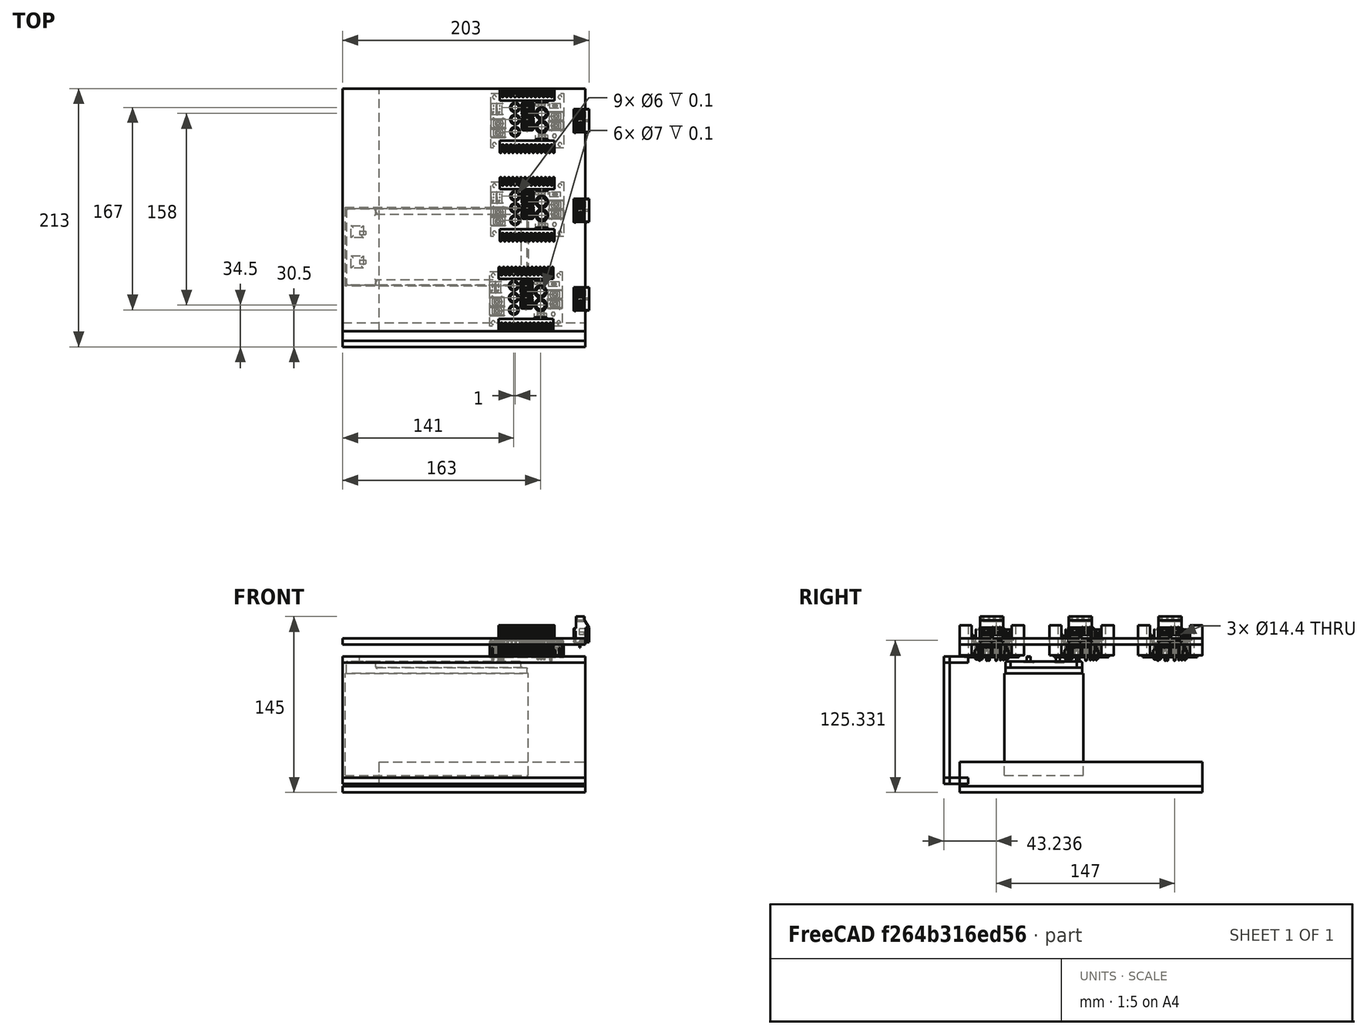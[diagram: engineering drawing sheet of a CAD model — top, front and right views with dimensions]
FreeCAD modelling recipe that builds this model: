
FCSTD DOCUMENT  (FreeCAD 0.20R29410 (Git))
Label: bateria
License: All rights reserved
LicenseURL: http://en.wikipedia.org/wiki/All_rights_reserved
objects: Part::Feature×14, Part::Box×9, App::Part×4, Part::Compound2×2, App::LinkGroup×2
note: 23 computed .brp shape members not serialized (recipe doc carries the construction recipe); baked Part::Feature solids carry a one-line shape summary decoded from their .brp

FEATURE [Part::Feature] Solid
  shape: bbox 151 x 65 x 84 mm, 6 faces (baked)
FEATURE [Part::Feature] Solid001
  shape: bbox 149 x 66.87 x 10.01 mm, 40 faces (baked)
FEATURE [Part::Feature] Solid002
  shape: bbox 5.1 x 3.056 x 5 mm, 9 faces (baked)
FEATURE [Part::Feature] Solid003
  shape: bbox 5.1 x 3.056 x 5 mm, 9 faces (baked)
FEATURE [Part::Compound2] Compound  label="Battery 2"
  Links = -> [Solid,Solid001,Solid002,Solid003]
  Placement = pos=(0,68,0) rot=(0,0,1;0rad)
FEATURE [Part::Feature] Feature  label="Regulator 5V"
  Placement = pos=(119,-98,99) rot=(1,0,0;1.5708rad)
  shape: bbox 60.01 x 53.01 x 29.46 mm, 1816 faces, 53 solids (baked)
FEATURE [Part::Feature] Solid004
  shape: bbox 151 x 65 x 84 mm, 6 faces (baked)
FEATURE [Part::Feature] Solid005
  shape: bbox 149 x 66.87 x 10.01 mm, 40 faces (baked)
FEATURE [Part::Feature] Solid006
  shape: bbox 5.1 x 3.056 x 5 mm, 9 faces (baked)
FEATURE [Part::Feature] Solid007
  shape: bbox 5.1 x 3.056 x 5 mm, 9 faces (baked)
FEATURE [Part::Compound2] Compound001  label="Battery 1"
  Links = -> [Solid004,Solid005,Solid006,Solid007]
FEATURE [App::LinkGroup] LinkGroup  label="Batteries"
  ElementList = -> [Compound001,Compound]
  LinkMode = 0
  Placement = pos=(-7.62939e-06,9.53674e-07,-7) rot=(0,0,1;0rad)
FEATURE [Part::Feature] Feature001  label="Regulator 12V"
  Placement = pos=(120,-24,99) rot=(1,0,0;1.5708rad)
  shape: bbox 60.01 x 53.01 x 29.46 mm, 1816 faces, 53 solids (baked)
FEATURE [Part::Feature] Feature002  label="Regulator 19V"
  Placement = pos=(120,49,99) rot=(1,0,0;1.5708rad)
  shape: bbox 60.01 x 53.01 x 29.46 mm, 1816 faces, 53 solids (baked)
FEATURE [Part::Box] Box  label="Cube"
  AttacherType = Attacher::AttachEngine3D
  Height = 5
  Length = 200
  Placement = pos=(-2,-102,108) rot=(0,0,1;0rad)
  Width = 200
FEATURE [App::Part] Part  label="Upper cover001"
  Group = -> [Box]
  Origin = -> Origin
  Placement = pos=(0,0,-9) rot=(0,0,1;0rad)
FEATURE [Part::Box] Box001  label="Cube004"
  AttacherType = Attacher::AttachEngine3D
  Height = 5
  Length = 200
  Placement = pos=(-2,-102,-14) rot=(0,0,1;0rad)
  Width = 200
FEATURE [Part::Box] Box002  label="Cube001"
  AttacherType = Attacher::AttachEngine3D
  Height = 105
  Length = 200
  Placement = pos=(-2,-115,-7) rot=(0,0,1;0rad)
  Width = 5
FEATURE [Part::Box] Box003  label="Cube002"
  AttacherType = Attacher::AttachEngine3D
  Height = 5
  Length = 200
  Placement = pos=(-2,-115,-7) rot=(0,0,1;0rad)
  Width = 20
FEATURE [Part::Box] Box004  label="Cube003"
  AttacherType = Attacher::AttachEngine3D
  Height = 5
  Length = 200
  Placement = pos=(-2,-115,93) rot=(0,0,1;0rad)
  Width = 20
FEATURE [App::Part] Part001  label="Vertical Wall 1"
  Group = -> [Box002,Box003,Box004]
  Origin = -> Origin001
  Placement = pos=(0,13,0) rot=(0,0,1;0rad)
FEATURE [Part::Box] Box005  label="Cube005"
  AttacherType = Attacher::AttachEngine3D
  Height = 105
  Length = 200
  Placement = pos=(-2,-115,-7) rot=(0,0,1;0rad)
  Width = 5
FEATURE [Part::Box] Box006  label="Cube006"
  AttacherType = Attacher::AttachEngine3D
  Height = 5
  Length = 200
  Placement = pos=(-2,-115,-7) rot=(0,0,1;0rad)
  Width = 20
FEATURE [Part::Box] Box007  label="Cube007"
  AttacherType = Attacher::AttachEngine3D
  Height = 5
  Length = 200
  Placement = pos=(-2,-115,93) rot=(0,0,1;0rad)
  Width = 20
FEATURE [App::Part] Part003  label="Vertical Wall 002"
  Group = -> [Box005,Box006,Box007]
  Origin = -> Origin003
  Placement = pos=(0,-16,91) rot=(1,0,0;3.14159rad)
FEATURE [Part::Box] Box008  label="Cube008"
  AttacherType = Attacher::AttachEngine3D
  Height = 20
  Length = 170
  Placement = pos=(28,-102,-9) rot=(0,0,1;0rad)
  Width = 200
FEATURE [App::Part] Part002  label="Lower support"
  Group = -> [Box001,Box008]
  Origin = -> Origin002
FEATURE [Part::Feature] Feature004  label="BR1102V"
  Placement = pos=(201,-12,110) rot=(0,0,1;3.14159rad)
  shape: bbox 12.7 x 19.5 x 25.5 mm, 126 faces, 7 solids (baked)
FEATURE [Part::Feature] Feature005  label="BR1102V001"
  Placement = pos=(201,-85,110) rot=(0,0,1;3.14159rad)
  shape: bbox 12.7 x 19.5 x 25.5 mm, 126 faces, 7 solids (baked)
FEATURE [Part::Feature] Feature006  label="BR1102V002"
  Placement = pos=(201,62,110) rot=(0,0,1;3.14159rad)
  shape: bbox 12.7 x 19.5 x 25.5 mm, 126 faces, 7 solids (baked)
FEATURE [App::LinkGroup] LinkGroup001  label="Regulators"
  ElementList = -> [Feature,Feature001,Feature002,Feature004,Feature005,Feature006]
  LinkMode = 0
  Placement = pos=(-29,2.38419e-06,11) rot=(0,0,1;0rad)
